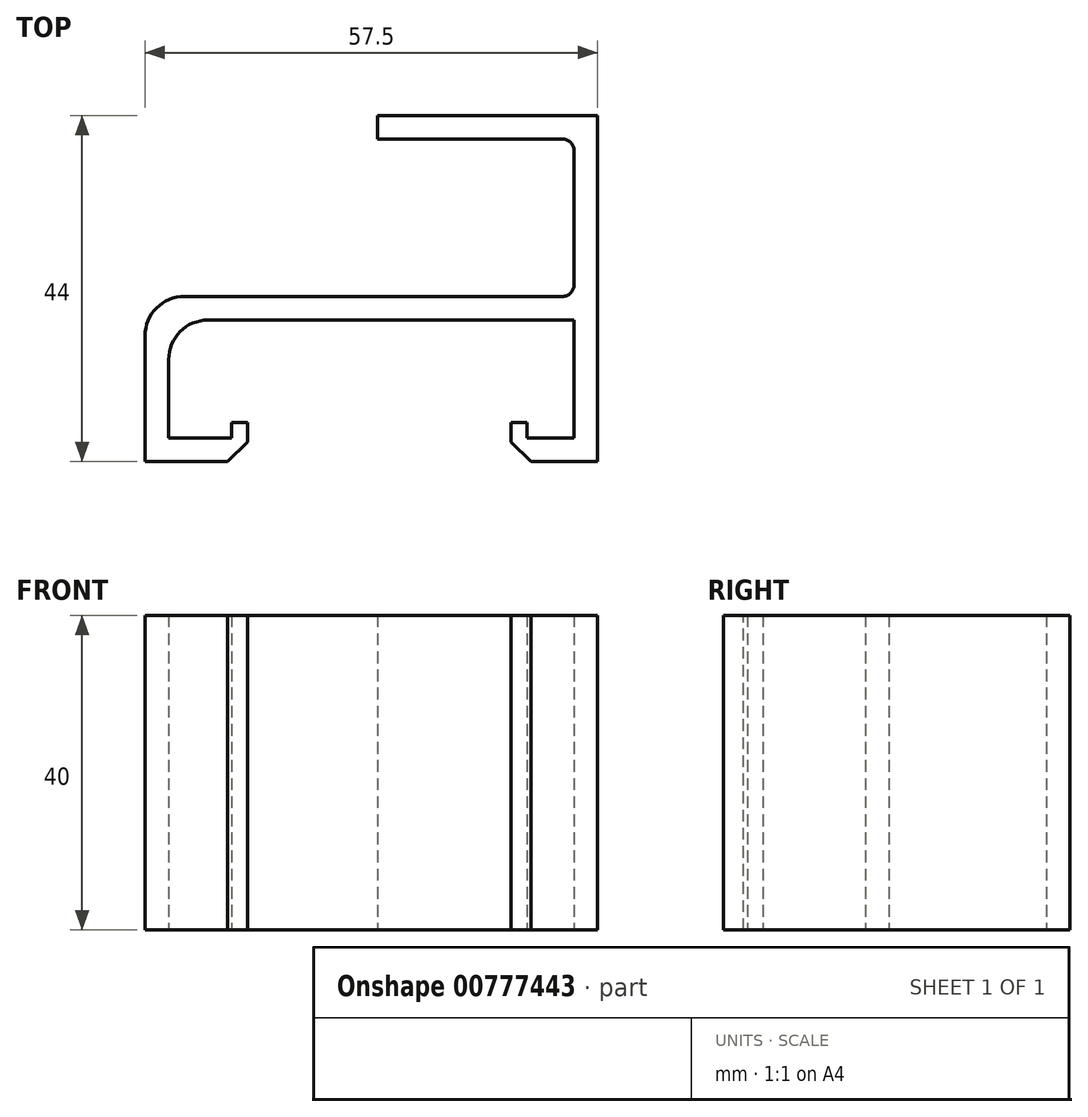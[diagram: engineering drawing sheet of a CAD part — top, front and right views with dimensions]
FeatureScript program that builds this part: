
annotation { "Feature Type Name" : "Feature", "Feature Type Description" : "" }
export const myFeature = defineFeature(function(context is Context, id is Id, definition is map)
    precondition{}
    {
        {
            var Q0;
            Q0=qCreatedBy(makeId("Top.planeOp"),FACE);
            var sketch = newSketch(context, id + "F0", { "sketchPlane" : qUnion([Q0])});
            skLineSegment(sketch, "E0", {"start": v(0, 0) * mm, "end": v(0, 18) * mm});
            skLineSegment(sketch, "E1", {"start": v(0, 18) * mm, "end": v(0, 18) * mm});
            skLineSegment(sketch, "E2", {"start": v(0, 18) * mm, "end": v(0, 41) * mm});
            skLineSegment(sketch, "E3", {"start": v(0, 41) * mm, "end": v(-28, 41) * mm});
            skLineSegment(sketch, "E4", {"start": v(-28, 41) * mm, "end": v(-28, 38) * mm});
            skLineSegment(sketch, "E5", {"start": v(-28, 38) * mm, "end": v(-3, 38) * mm});
            skLineSegment(sketch, "E6", {"start": v(-3, 38) * mm, "end": v(-3, 18) * mm});
            skLineSegment(sketch, "E7", {"start": v(-3, 18) * mm, "end": v(-52.5, 18) * mm});
            skLineSegment(sketch, "E8", {"start": v(-57.5, 13) * mm, "end": v(-57.5, -3) * mm});
            skLineSegment(sketch, "E9", {"start": v(-53, -3) * mm, "end": v(-44.5, -3) * mm});
            skLineSegment(sketch, "E10", {"start": v(-44.5, -3) * mm, "end": v(-44.5, 0) * mm});
            skLineSegment(sketch, "E11", {"start": v(-46.5, 0) * mm, "end": v(-54.5, 0) * mm});
            skLineSegment(sketch, "E12", {"start": v(-54.5, 0) * mm, "end": v(-54.5, 10) * mm});
            skLineSegment(sketch, "E13", {"start": v(-49.5, 15) * mm, "end": v(-3, 15) * mm});
            skLineSegment(sketch, "E14", {"start": v(-3, 15) * mm, "end": v(-3, 0) * mm});
            skLineSegment(sketch, "E15", {"start": v(-9, 0) * mm, "end": v(-3, 0) * mm});
            skLineSegment(sketch, "E16", {"start": v(0, 0) * mm, "end": v(0, -3) * mm});
            skLineSegment(sketch, "E17", {"start": v(0, -3) * mm, "end": v(-11, -3) * mm});
            skLineSegment(sketch, "E18", {"start": v(-11, -3) * mm, "end": v(-11, 0) * mm});
            skPoint(sketch, "E19.visualSharp", {"position": v(-54.5, 15) * mm});
            skArc(sketch, "E19.filletArc", {"start": v(-49.5, 15) * mm, "mid": v(-53.04, 13.54) * mm, "end": v(-54.5, 10) * mm});
            skPoint(sketch, "E20.visualSharp", {"position": v(-57.5, 18) * mm});
            skArc(sketch, "E20.filletArc", {"start": v(-52.5, 18) * mm, "mid": v(-56.04, 16.54) * mm, "end": v(-57.5, 13) * mm});
            skLineSegment(sketch, "E21", {"start": v(-46.5, 0) * mm, "end": v(-46.5, 2) * mm});
            skLineSegment(sketch, "E22", {"start": v(-46.5, 2) * mm, "end": v(-44.5, 2) * mm});
            skLineSegment(sketch, "E23", {"start": v(-44.5, 2) * mm, "end": v(-44.5, 0) * mm});
            skLineSegment(sketch, "E24", {"start": v(-11, 0) * mm, "end": v(-11, 2) * mm});
            skLineSegment(sketch, "E25", {"start": v(-11, 2) * mm, "end": v(-9, 2) * mm});
            skLineSegment(sketch, "E26", {"start": v(-9, 2) * mm, "end": v(-9, 0) * mm});
            skLineSegment(sketch, "E27", {"start": v(-57.5, -3) * mm, "end": v(-53, -3) * mm});
            skSolve(sketch);
        }
        {
            var Q0;
            Q0=makeQuery(id+"F0.imprint","IMPRINT",FACE,{"disambiguationData":[TD([[makeQuery(id+"F0.imprint","IMPRINT",EDGE,{"derivedFrom":sQuery(id+"F0.wireOp",EDGE,"E0")}),1.0]])]});
            extrude(context, id + "F1", {"entities" : qUnion([Q0]), "depth" : 40 * mm, "offsetDistance" : 25 * mm});
        }
        {
            var Q0;
            Q0=makeQuery(id+"F1.opExtrude","SWEPT_EDGE",EDGE,{"disambiguationData":[OSD([sQuery(id+"F0.wireOp",EDGE,"E17"),sQuery(id+"F0.wireOp",EDGE,"E18")])]});
            var Q1;
            Q1=makeQuery(id+"F1.opExtrude","SWEPT_EDGE",EDGE,{"disambiguationData":[OSD([sQuery(id+"F0.wireOp",EDGE,"E9"),sQuery(id+"F0.wireOp",EDGE,"E10")])]});
            chamfer(context, id + "F2", {"entities" : qUnion([Q0, Q1]), "width" : 2.5 * mm, "tangentPropagation" : true});
        }
        {
            var Q0;
            Q0=makeQuery(id+"F1.opExtrude","SWEPT_EDGE",EDGE,{"disambiguationData":[OSD([sQuery(id+"F0.wireOp",EDGE,"E6"),sQuery(id+"F0.wireOp",EDGE,"E7")])]});
            var Q1;
            Q1=makeQuery(id+"F1.opExtrude","SWEPT_EDGE",EDGE,{"disambiguationData":[OSD([sQuery(id+"F0.wireOp",EDGE,"E5"),sQuery(id+"F0.wireOp",EDGE,"E6")])]});
            fillet(context, id + "F3", {"entities" : qUnion([Q0, Q1]), "radius" : 1.5 * mm, "tangentPropagation" : true, "allowEdgeOverflow" : false});
        }
    });
